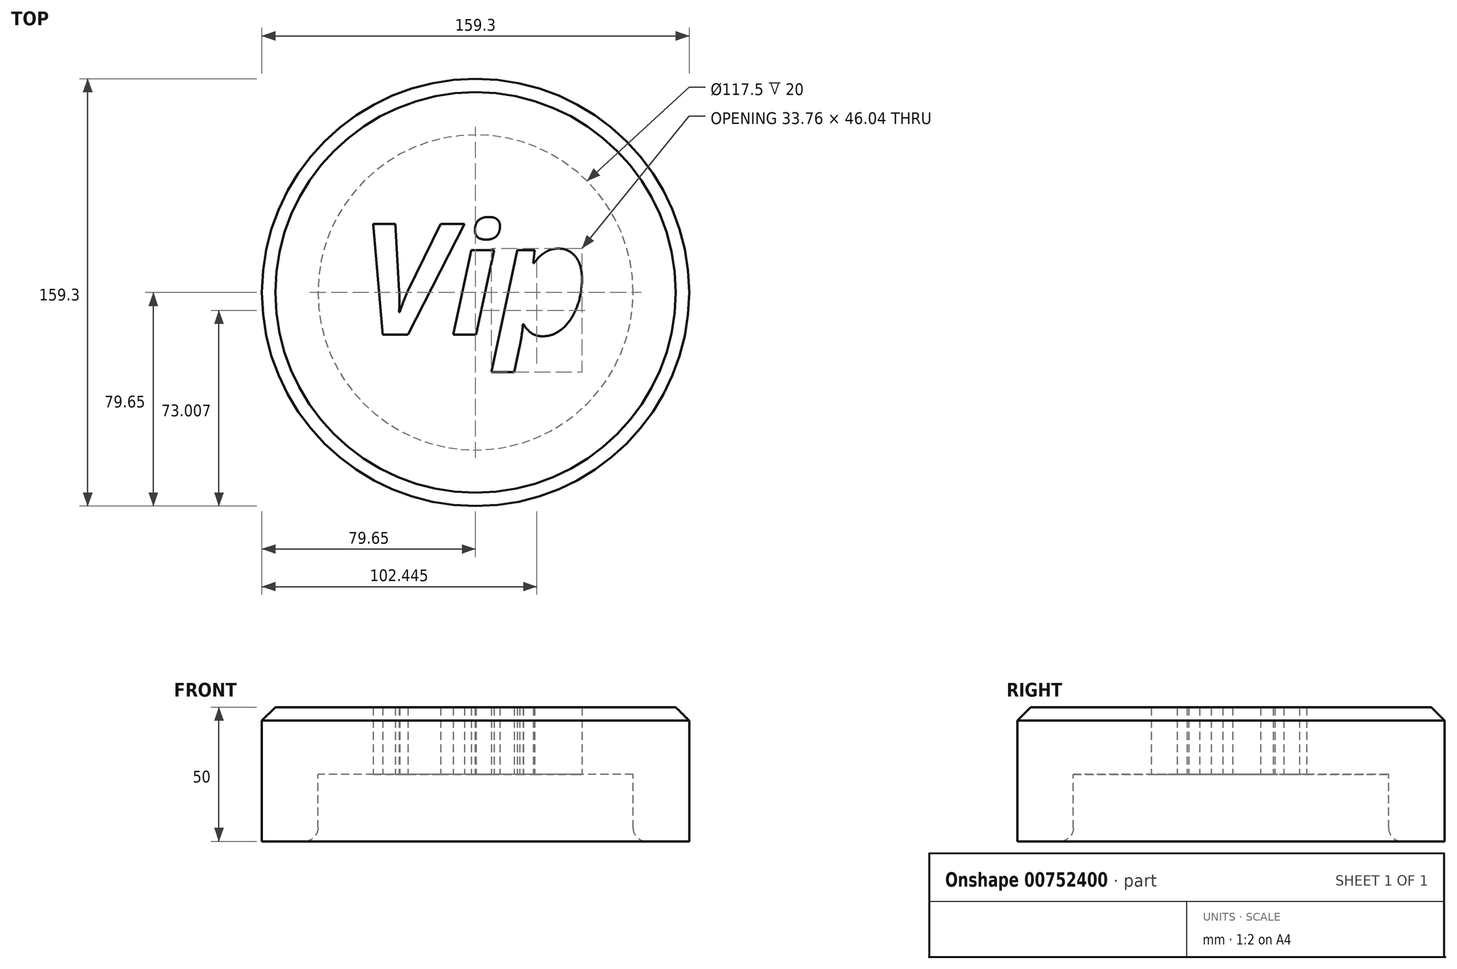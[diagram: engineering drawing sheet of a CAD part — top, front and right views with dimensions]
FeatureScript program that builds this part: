
annotation { "Feature Type Name" : "Feature", "Feature Type Description" : "" }
export const myFeature = defineFeature(function(context is Context, id is Id, definition is map)
    precondition{}
    {
        {
            var Q0;
            Q0=qCreatedBy(makeId("Top.planeOp"),FACE);
            var sketch = newSketch(context, id + "F0", { "sketchPlane" : qUnion([Q0])});
            skCircle(sketch, "E0", {"center": v(0, 0) * mm, "radius": 58.75 * mm});
            skLineSegment(sketch, "E1", {"start": v(-58.75, 0) * mm, "end": v(-58.75, -72.81) * mm});
            skLineSegment(sketch, "E2", {"start": v(58.75, 0) * mm, "end": v(58.75, -73.07) * mm});
            skLineSegment(sketch, "E3", {"start": v(58.75, -73.07) * mm, "end": v(-58.75, -72.81) * mm});
            skText(sketch, "E4", { "text": "Vip", "fontName": "OpenSans-BoldItalic.ttf"});
            const initialGuessF0  = {"E4": [-0.04342, -0.01577, 1, 0, 0.04162]};
            skSetInitialGuess(sketch, initialGuessF0);
            skSolve(sketch);
        }
        {
            var Q0;
            Q0=makeQuery(id+"F0.imprint","IMPRINT",FACE,{"disambiguationData":[TD([[makeQuery(id+"F0.imprint","IMPRINT",EDGE,{"derivedFrom":sQuery(id+"F0.wireOp",EDGE,"E4.sketch_text.stroke-0")}),1.0]])]});
            extrude(context, id + "F1", {"entities" : qUnion([Q0]), "depth" : 25 * mm, "offsetDistance" : 25 * mm});
        }
        {
            var Q0;
            Q0=makeQuery(id+"F1.opExtrude","CAP_FACE",FACE,{"disambiguationData":[OSD([sQuery(id+"F0.wireOp",EDGE,"E0"),sQuery(id+"F0.wireOp",EDGE,"E4.sketch_text.stroke-0"),sQuery(id+"F0.wireOp",EDGE,"E4.sketch_text.stroke-1"),sQuery(id+"F0.wireOp",EDGE,"E4.sketch_text.stroke-2"),sQuery(id+"F0.wireOp",EDGE,"E4.sketch_text.stroke-3"),sQuery(id+"F0.wireOp",EDGE,"E4.sketch_text.stroke-4"),sQuery(id+"F0.wireOp",EDGE,"E4.sketch_text.stroke-5"),sQuery(id+"F0.wireOp",EDGE,"E4.sketch_text.stroke-6"),sQuery(id+"F0.wireOp",EDGE,"E4.sketch_text.stroke-7"),sQuery(id+"F0.wireOp",EDGE,"E4.sketch_text.stroke-8"),sQuery(id+"F0.wireOp",EDGE,"E4.sketch_text.stroke-9"),sQuery(id+"F0.wireOp",EDGE,"E4.sketch_text.stroke-10"),sQuery(id+"F0.wireOp",EDGE,"E4.sketch_text.stroke-11"),sQuery(id+"F0.wireOp",EDGE,"E4.sketch_text.stroke-12"),sQuery(id+"F0.wireOp",EDGE,"E4.sketch_text.stroke-13"),sQuery(id+"F0.wireOp",EDGE,"E4.sketch_text.stroke-14"),sQuery(id+"F0.wireOp",EDGE,"E4.sketch_text.stroke-15"),sQuery(id+"F0.wireOp",EDGE,"E4.sketch_text.stroke-16"),sQuery(id+"F0.wireOp",EDGE,"E4.sketch_text.stroke-17"),sQuery(id+"F0.wireOp",EDGE,"E4.sketch_text.stroke-18"),sQuery(id+"F0.wireOp",EDGE,"E4.sketch_text.stroke-19"),sQuery(id+"F0.wireOp",EDGE,"E4.sketch_text.stroke-20"),sQuery(id+"F0.wireOp",EDGE,"E4.sketch_text.stroke-21"),sQuery(id+"F0.wireOp",EDGE,"E4.sketch_text.stroke-22"),sQuery(id+"F0.wireOp",EDGE,"E4.sketch_text.stroke-23"),sQuery(id+"F0.wireOp",EDGE,"E4.sketch_text.stroke-24"),sQuery(id+"F0.wireOp",EDGE,"E4.sketch_text.stroke-25"),sQuery(id+"F0.wireOp",EDGE,"E4.sketch_text.stroke-26"),sQuery(id+"F0.wireOp",EDGE,"E4.sketch_text.stroke-27"),sQuery(id+"F0.wireOp",EDGE,"E4.sketch_text.stroke-28"),sQuery(id+"F0.wireOp",EDGE,"E4.sketch_text.stroke-29"),sQuery(id+"F0.wireOp",EDGE,"E4.sketch_text.stroke-30"),sQuery(id+"F0.wireOp",EDGE,"E4.sketch_text.stroke-31"),sQuery(id+"F0.wireOp",EDGE,"E4.sketch_text.stroke-32"),sQuery(id+"F0.wireOp",EDGE,"E4.sketch_text.stroke-33"),sQuery(id+"F0.wireOp",EDGE,"E4.sketch_text.stroke-34"),sQuery(id+"F0.wireOp",EDGE,"E4.sketch_text.stroke-35"),sQuery(id+"F0.wireOp",EDGE,"E4.sketch_text.stroke-36"),sQuery(id+"F0.wireOp",EDGE,"E4.sketch_text.stroke-37")])],"isStart":false});
            var sketch = newSketch(context, id + "F2", { "sketchPlane" : qUnion([Q0])});
            skCircle(sketch, "E5.0", {"center": v(0, 0) * mm, "radius": 79.65 * mm});
            skSolve(sketch);
        }
        {
            var Q0;
            Q0=makeQuery(id+"F2.imprint","IMPRINT",FACE,{"disambiguationData":[TD([[makeQuery(id+"F2.imprint","IMPRINT",EDGE,{"derivedFrom":sQuery(id+"F2.wireOp",EDGE,"E5.0")}),1.0]])]});
            extrude(context, id + "F3", {"entities" : qUnion([Q0]), "operationType" : NewBodyOperationType.ADD, "oppositeDirection" : true, "depth" : 50 * mm, "offsetDistance" : 25 * mm});
        }
        {
            var Q0;
            Q0=makeQuery(id+"F3.opExtrude","CAP_EDGE",EDGE,{"disambiguationData":[OSD([sQuery(id+"F2.wireOp",EDGE,"E5.0")])],"isStart":true});
            chamfer(context, id + "F4", {"entities" : qUnion([Q0]), "width" : 5 * mm, "tangentPropagation" : true});
        }
        {
            var Q0;
            Q0=makeQuery(id+"F3.opExtrude","CAP_EDGE",EDGE,{"disambiguationData":[OSD([sQuery(id+"F0.wireOp",EDGE,"E0")])],"isStart":false});
            fillet(context, id + "F5", {"entities" : qUnion([Q0]), "radius" : 5 * mm, "tangentPropagation" : true, "allowEdgeOverflow" : false});
        }
    });
